FCSTD DOCUMENT  (FreeCAD 0.21R33694 (Git))
Label: OJT1_T018_R02_ HOLA
License: All rights reserved
LicenseURL: http://en.wikipedia.org/wiki/All_rights_reserved
objects: Sketcher::SketchObject×4, PartDesign::Body×1
note: 5 computed .brp shape members not serialized (recipe doc carries the construction recipe); baked Part::Feature solids carry a one-line shape summary decoded from their .brp

FEATURE [Sketcher::SketchObject] Sketch
  FullyConstrained = false
  MapMode = 5
  Support = -> [XY_Plane]
  sketch-geometry (12):
    g0: LineSegment StartX=-39.704 StartY=30.0822 StartZ=0 EndX=-29.704 EndY=30.0822 EndZ=0
    g1: LineSegment StartX=-29.704 StartY=30.0822 StartZ=0 EndX=-29.704 EndY=-19.9178 EndZ=0
    g2: LineSegment StartX=-29.704 StartY=-19.9178 StartZ=0 EndX=-39.704 EndY=-19.9178 EndZ=0
    g3: LineSegment StartX=-39.704 StartY=-19.9178 StartZ=0 EndX=-39.704 EndY=30.0822 EndZ=0
    g4: LineSegment StartX=-19.704 StartY=30.373 StartZ=0 EndX=-9.70399 EndY=30.373 EndZ=0
    g5: LineSegment StartX=-9.70399 StartY=30.373 StartZ=0 EndX=-9.70399 EndY=-19.627 EndZ=0
    g6: LineSegment StartX=-9.70399 StartY=-19.627 StartZ=0 EndX=-19.704 EndY=-19.627 EndZ=0
    g7: LineSegment StartX=-19.704 StartY=-19.627 StartZ=0 EndX=-19.704 EndY=30.373 EndZ=0
    g8: LineSegment StartX=-29.704 StartY=9.58003 StartZ=0 EndX=-19.704 EndY=9.58003 EndZ=0
    g9: LineSegment StartX=-19.704 StartY=9.58003 StartZ=0 EndX=-19.704 EndY=0 EndZ=0
    g10: LineSegment StartX=-19.704 StartY=0 StartZ=0 EndX=-29.704 EndY=0 EndZ=0
    g11: LineSegment StartX=-29.704 StartY=0 StartZ=0 EndX=-29.704 EndY=9.58003 EndZ=0
  constraints (33):
    c: Coincident(g0,g1)
    c: Coincident(g1,g2)
    c: Coincident(g2,g3)
    c: Coincident(g3,g0)
    c: Horizontal(g0)
    c: Horizontal(g2)
    c: Vertical(g1)
    c: Vertical(g3)
    c: DistanceY(g3,g3) = 50
    c: DistanceX(g0,g0) = 10
    c: Coincident(g4,g5)
    c: Coincident(g5,g6)
    c: Coincident(g6,g7)
    c: Coincident(g7,g4)
    c: Horizontal(g4)
    c: Horizontal(g6)
    c: Vertical(g5)
    c: Vertical(g7)
    c: Equal(g7,g1)
    c: Equal(g1,g7)
    c: DistanceX(g4,g4) = 10
    c: Coincident(g8,g9)
    c: Coincident(g9,g10)
    c: Coincident(g10,g11)
    c: Coincident(g11,g8)
    c: Horizontal(g8)
    c: Horizontal(g10)
    c: Vertical(g9)
    c: Vertical(g11)
    c: PointOnObject(g9,g-1)
    c: PointOnObject(g8,g1)
    c: PointOnObject(g8,g7)
    c: DistanceX(g8,g8) = 10
FEATURE [Sketcher::SketchObject] Sketch001
  FullyConstrained = false
  MapMode = 5
  Support = -> [XY_Plane]
  sketch-geometry (8):
    g0: LineSegment StartX=0.548315 StartY=29.7047 StartZ=0 EndX=0.548315 EndY=-20.2953 EndZ=0
    g1: LineSegment StartX=0.548315 StartY=-20.2953 StartZ=0 EndX=30.5483 EndY=-20.2953 EndZ=0
    g2: LineSegment StartX=30.5483 StartY=-20.2953 StartZ=0 EndX=30.5483 EndY=29.7047 EndZ=0
    g3: LineSegment StartX=30.5483 StartY=29.7047 StartZ=0 EndX=0.548315 EndY=29.7047 EndZ=0
    g4: LineSegment StartX=10.147 StartY=19.7659 StartZ=0 EndX=20.147 EndY=19.7659 EndZ=0
    g5: LineSegment StartX=20.147 StartY=19.7659 StartZ=0 EndX=20.147 EndY=-9.75143 EndZ=0
    g6: LineSegment StartX=20.147 StartY=-9.75143 StartZ=0 EndX=10.147 EndY=-9.75143 EndZ=0
    g7: LineSegment StartX=10.147 StartY=-9.75143 StartZ=0 EndX=10.147 EndY=19.7659 EndZ=0
  constraints (19):
    c: Vertical(g0)
    c: Coincident(g1,g0)
    c: Horizontal(g1)
    c: Coincident(g2,g1)
    c: Vertical(g2)
    c: Coincident(g3,g2)
    c: Coincident(g3,g0)
    c: Horizontal(g3)
    c: Coincident(g4,g5)
    c: Coincident(g5,g6)
    c: Coincident(g6,g7)
    c: Coincident(g7,g4)
    c: Horizontal(g4)
    c: Horizontal(g6)
    c: Vertical(g5)
    c: Vertical(g7)
    c: DistanceY(g0,g0) = 50
    c: DistanceX(g4,g4) = 10
    c: DistanceX(g3,g3) = 30
FEATURE [Sketcher::SketchObject] Sketch002
  FullyConstrained = false
  MapMode = 5
  Support = -> [XY_Plane]
  sketch-geometry (8):
    g0: LineSegment StartX=40.2583 StartY=30.1141 StartZ=0 EndX=50.2583 EndY=30.1141 EndZ=0
    g1: LineSegment StartX=50.2583 StartY=30.1141 StartZ=0 EndX=50.2583 EndY=-19.8859 EndZ=0
    g2: LineSegment StartX=50.2583 StartY=-19.8859 StartZ=0 EndX=40.2583 EndY=-19.8859 EndZ=0
    g3: LineSegment StartX=40.2583 StartY=-19.8859 StartZ=0 EndX=40.2583 EndY=30.1141 EndZ=0
    g4: LineSegment StartX=50.2583 StartY=-9.91887 StartZ=0 EndX=70.2583 EndY=-9.91887 EndZ=0
    g5: LineSegment StartX=70.2583 StartY=-9.91887 StartZ=0 EndX=70.2583 EndY=-19.9189 EndZ=0
    g6: LineSegment StartX=70.2583 StartY=-19.9189 StartZ=0 EndX=50.2583 EndY=-19.9189 EndZ=0
    g7: LineSegment StartX=50.2583 StartY=-19.9189 StartZ=0 EndX=50.2583 EndY=-9.91887 EndZ=0
  constraints (21):
    c: Coincident(g0,g1)
    c: Coincident(g1,g2)
    c: Coincident(g2,g3)
    c: Coincident(g3,g0)
    c: Horizontal(g0)
    c: Horizontal(g2)
    c: Vertical(g1)
    c: Vertical(g3)
    c: Coincident(g4,g5)
    c: Coincident(g5,g6)
    c: Coincident(g6,g7)
    c: Coincident(g7,g4)
    c: Horizontal(g4)
    c: Horizontal(g6)
    c: Vertical(g5)
    c: Vertical(g7)
    c: PointOnObject(g4,g1)
    c: DistanceY(g1,g1) = 50
    c: DistanceX(g0,g0) = 10
    c: DistanceX(g4,g4) = 20
    c: DistanceY(g5,g5) = 10
FEATURE [Sketcher::SketchObject] Sketch003
  FullyConstrained = false
  MapMode = 5
  Support = -> [XY_Plane]
  sketch-geometry (12):
    g0: LineSegment StartX=80.128 StartY=29.5885 StartZ=0 EndX=80.128 EndY=-20.0861 EndZ=0
    g1: LineSegment StartX=80.128 StartY=-20.0861 StartZ=0 EndX=90.128 EndY=-20.0861 EndZ=0
    g2: LineSegment StartX=90.128 StartY=-20.0861 StartZ=0 EndX=90.128 EndY=-2.2987 EndZ=0
    g3: LineSegment StartX=90.128 StartY=-2.2987 StartZ=0 EndX=100.128 EndY=-2.51562 EndZ=0
    g4: LineSegment StartX=100.128 StartY=-2.51562 StartZ=0 EndX=100.128 EndY=-20.0861 EndZ=0
    g5: LineSegment StartX=100.128 StartY=-20.0861 StartZ=0 EndX=110.128 EndY=-20.0861 EndZ=0
    g6: LineSegment StartX=110.128 StartY=-20.0861 StartZ=0 EndX=110.128 EndY=29.5885 EndZ=0
    g7: LineSegment StartX=110.128 StartY=29.5885 StartZ=0 EndX=80.128 EndY=29.5885 EndZ=0
    g8: LineSegment StartX=89.8694 StartY=19.8271 StartZ=0 EndX=99.8694 EndY=19.8271 EndZ=0
    g9: LineSegment StartX=99.8694 StartY=19.8271 StartZ=0 EndX=99.8694 EndY=9.84881 EndZ=0
    g10: LineSegment StartX=99.8694 StartY=9.84881 StartZ=0 EndX=89.8694 EndY=9.84881 EndZ=0
    g11: LineSegment StartX=89.8694 StartY=9.84881 StartZ=0 EndX=89.8694 EndY=19.8271 EndZ=0
  constraints (26):
    c: Vertical(g0)
    c: Coincident(g1,g0)
    c: Coincident(g2,g1)
    c: Vertical(g2)
    c: Coincident(g3,g2)
    c: Coincident(g4,g3)
    c: Vertical(g4)
    c: Coincident(g5,g4)
    c: Horizontal(g5)
    c: Coincident(g6,g5)
    c: Vertical(g6)
    c: Coincident(g7,g6)
    c: Coincident(g7,g0)
    c: Horizontal(g7)
    c: Coincident(g8,g9)
    c: Coincident(g9,g10)
    c: Coincident(g10,g11)
    c: Coincident(g11,g8)
    c: Horizontal(g8)
    c: Horizontal(g10)
    c: Vertical(g9)
    c: Vertical(g11)
    c: DistanceX(g10,g10) = 10
    c: DistanceX(g7,g7) = 30
    c: DistanceX(g1,g1) = 10
    c: DistanceX(g5,g5) = 10
FEATURE [PartDesign::Body] Body
  Group = -> [Sketch,Sketch001,Sketch002,Sketch003]
  Origin = -> Origin
